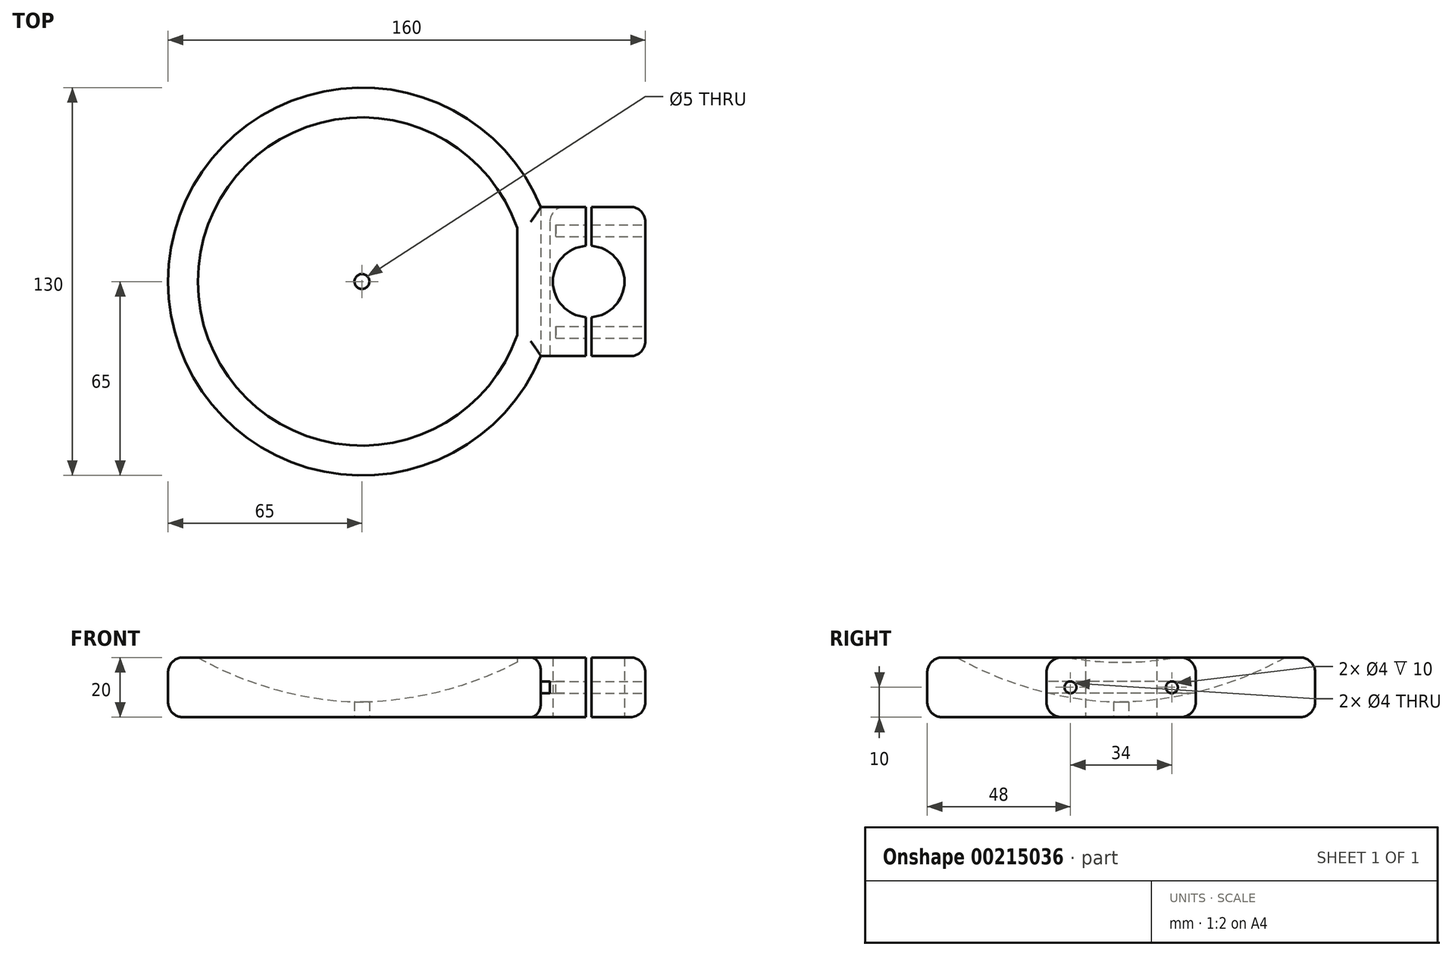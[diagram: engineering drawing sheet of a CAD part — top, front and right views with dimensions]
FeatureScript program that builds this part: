
annotation { "Feature Type Name" : "Feature", "Feature Type Description" : "" }
export const myFeature = defineFeature(function(context is Context, id is Id, definition is map)
    precondition{}
    {
        {
            var Q0;
            Q0=qCreatedBy(makeId("Front.planeOp"),FACE);
            var sketch = newSketch(context, id + "F0", { "sketchPlane" : qUnion([Q0])});
            skLineSegment(sketch, "E0", {"start": v(0, 0) * mm, "end": v(65, 0) * mm});
            skLineSegment(sketch, "E1", {"start": v(65, 0) * mm, "end": v(65, 20) * mm});
            skLineSegment(sketch, "E2", {"start": v(65, 20) * mm, "end": v(55, 20) * mm});
            skArc(sketch, "E3", {"start": v(0, 5) * mm, "mid": v(28.42, 9.13) * mm, "end": v(55, 20) * mm});
            skLineSegment(sketch, "E4", {"start": v(0, 5) * mm, "end": v(0, 0) * mm});
            skPoint(sketch, "E5.end.orphan", {"position": v(-65, 0) * mm});
            skPoint(sketch, "E6.visualSharp", {"position": v(65, 0) * mm});
            skPoint(sketch, "E7.visualSharp", {"position": v(65, 20) * mm});
            skSolve(sketch);
        }
        {
            var Q0;
            Q0=makeQuery(id+"F0.imprint","IMPRINT",FACE,{"disambiguationData":[TD([[makeQuery(id+"F0.imprint","IMPRINT",EDGE,{"derivedFrom":sQuery(id+"F0.wireOp",EDGE,"E0")}),1.0]])]});
            var Q1;
            Q1=sQuery(id+"F0.wireOp",EDGE,"E4");
            revolve(context, id + "F1", {"surfaceOperationType" : NewSurfaceOperationType.NEW, "entities" : qUnion([Q0]), "axis" : qUnion([Q1]), "revolveType" : RevolveType.FULL});
        }
        {
            var Q0;
            Q0=makeQuery(id+"F1.opRevolve","SWEPT_EDGE",EDGE,{"disambiguationData":[OSD([sQuery(id+"F0.wireOp",EDGE,"E1"),sQuery(id+"F0.wireOp",EDGE,"E2")])]});
            var Q1;
            Q1=makeQuery(id+"F1.opRevolve","SWEPT_EDGE",EDGE,{"disambiguationData":[OSD([sQuery(id+"F0.wireOp",EDGE,"E0"),sQuery(id+"F0.wireOp",EDGE,"E1")])]});
            fillet(context, id + "F2", {"entities" : qUnion([Q0, Q1]), "radius" : 5 * mm, "tangentPropagation" : true, "allowEdgeOverflow" : false});
        }
        {
            var Q0;
            Q0=qCreatedBy(makeId("Top.planeOp"),FACE);
            var sketch = newSketch(context, id + "F3", { "sketchPlane" : qUnion([Q0])});
            skLineSegment(sketch, "E8.bottom", {"start": v(52, 25) * mm, "end": v(75, 25) * mm});
            skLineSegment(sketch, "E8.top", {"start": v(52, -25) * mm, "end": v(75, -25) * mm});
            skLineSegment(sketch, "E8.left", {"start": v(52, 25) * mm, "end": v(52, -25) * mm});
            skLineSegment(sketch, "E9.trimOffspring", {"start": v(75, 25) * mm, "end": v(75, -25) * mm});
            skSolve(sketch);
        }
        {
            var Q0;
            Q0=qSketchRegion(id+"F3",true);
            extrude(context, id + "F4", {"entities" : qUnion([Q0]), "operationType" : NewBodyOperationType.ADD, "depth" : 20 * mm});
        }
        {
            var Q0;
            Q0=qCreatedBy(makeId("Top.planeOp"),FACE);
            var sketch = newSketch(context, id + "F5", { "sketchPlane" : qUnion([Q0])});
            skCircle(sketch, "E10", {"center": v(76, 0) * mm, "radius": 12 * mm});
            skSolve(sketch);
        }
        {
            var Q0;
            Q0=qSketchRegion(id+"F5",true);
            extrude(context, id + "F6", {"entities" : qUnion([Q0]), "operationType" : NewBodyOperationType.REMOVE, "depth" : 25 * mm});
        }
        {
            var Q0;
            Q0=qCreatedBy(makeId("Top.planeOp"),FACE);
            var sketch = newSketch(context, id + "F7", { "sketchPlane" : qUnion([Q0])});
            skLineSegment(sketch, "E11.bottom", {"start": v(77, 25) * mm, "end": v(95, 25) * mm});
            skLineSegment(sketch, "E11.top", {"start": v(77, -25) * mm, "end": v(95, -25) * mm});
            skLineSegment(sketch, "E11.left", {"start": v(77, 25) * mm, "end": v(77, -25) * mm});
            skLineSegment(sketch, "E11.right", {"start": v(95, 25) * mm, "end": v(95, -25) * mm});
            skSolve(sketch);
        }
        {
            var Q0;
            Q0=qSketchRegion(id+"F7",true);
            extrude(context, id + "F8", {"entities" : qUnion([Q0]), "depth" : 20 * mm});
        }
        {
            var Q0;
            Q0=qCreatedBy(makeId("Top.planeOp"),FACE);
            var sketch = newSketch(context, id + "F9", { "sketchPlane" : qUnion([Q0])});
            skCircle(sketch, "E12", {"center": v(76, 0) * mm, "radius": 12 * mm});
            skSolve(sketch);
        }
        {
            var Q0;
            Q0=qSketchRegion(id+"F9",true);
            extrude(context, id + "F10", {"entities" : qUnion([Q0]), "operationType" : NewBodyOperationType.REMOVE, "depth" : 25 * mm});
        }
        {
            var Q0;
            Q0=makeQuery(id+"F8.opExtrude","CAP_EDGE",EDGE,{"disambiguationData":[OSD([sQuery(id+"F7.wireOp",EDGE,"E11.top")])],"isStart":false});
            var Q1;
            Q1=makeQuery(id+"F8.opExtrude","CAP_EDGE",EDGE,{"disambiguationData":[OSD([sQuery(id+"F7.wireOp",EDGE,"E11.top")])],"isStart":true});
            var Q2;
            Q2=makeQuery(id+"F8.opExtrude","CAP_EDGE",EDGE,{"disambiguationData":[OSD([sQuery(id+"F7.wireOp",EDGE,"E11.bottom")])],"isStart":false});
            var Q3;
            Q3=makeQuery(id+"F8.opExtrude","CAP_EDGE",EDGE,{"disambiguationData":[OSD([sQuery(id+"F7.wireOp",EDGE,"E11.bottom")])],"isStart":true});
            var Q4;
            Q4=makeQuery(id+"F8.opExtrude","CAP_EDGE",EDGE,{"disambiguationData":[OSD([sQuery(id+"F7.wireOp",EDGE,"E11.right")])],"isStart":false});
            var Q5;
            Q5=makeQuery(id+"F8.opExtrude","CAP_EDGE",EDGE,{"disambiguationData":[OSD([sQuery(id+"F7.wireOp",EDGE,"E11.right")])],"isStart":true});
            var Q6;
            Q6=makeQuery(id+"F8.opExtrude","SWEPT_EDGE",EDGE,{"disambiguationData":[OSD([sQuery(id+"F7.wireOp",EDGE,"E11.top"),sQuery(id+"F7.wireOp",EDGE,"E11.right")])]});
            var Q7;
            Q7=makeQuery(id+"F8.opExtrude","SWEPT_EDGE",EDGE,{"disambiguationData":[OSD([sQuery(id+"F7.wireOp",EDGE,"E11.bottom"),sQuery(id+"F7.wireOp",EDGE,"E11.right")])]});
            fillet(context, id + "F11", {"entities" : qUnion([Q0, Q1, Q2, Q3, Q4, Q5, Q6, Q7]), "radius" : 5 * mm, "tangentPropagation" : true, "allowEdgeOverflow" : false});
        }
        {
            var Q0;
            Q0=makeQuery(id+"F4.opExtrude","CAP_EDGE",EDGE,{"disambiguationData":[OSD([sQuery(id+"F3.wireOp",EDGE,"E8.top")])],"isStart":false});
            var Q1;
            Q1=makeQuery(id+"F4.opExtrude","CAP_EDGE",EDGE,{"disambiguationData":[OSD([sQuery(id+"F3.wireOp",EDGE,"E8.top")])],"isStart":true});
            var Q2;
            Q2=makeQuery(id+"F4.opExtrude","CAP_EDGE",EDGE,{"disambiguationData":[OSD([sQuery(id+"F3.wireOp",EDGE,"E8.bottom")])],"isStart":true});
            var Q3;
            Q3=makeQuery(id+"F4.opExtrude","CAP_EDGE",EDGE,{"disambiguationData":[OSD([sQuery(id+"F3.wireOp",EDGE,"E8.bottom")])],"isStart":false});
            fillet(context, id + "F12", {"entities" : qUnion([Q0, Q1, Q2, Q3]), "radius" : 5 * mm, "allowEdgeOverflow" : false});
        }
        {
            var Q0;
            Q0=makeQuery(id+"F8.opExtrude","SWEPT_FACE",FACE,{"disambiguationData":[OSD([sQuery(id+"F7.wireOp",EDGE,"E11.right")])]});
            var sketch = newSketch(context, id + "F13", { "sketchPlane" : qUnion([Q0])});
            skCircle(sketch, "E13", {"center": v(-17, 10) * mm, "radius": 2 * mm});
            skCircle(sketch, "E14.MirrorC", {"center": v(17, 10) * mm, "radius": 2 * mm});
            skSolve(sketch);
        }
        {
            var Q0;
            Q0=qSketchRegion(id+"F13",true);
            extrude(context, id + "F14", {"entities" : qUnion([Q0]), "operationType" : NewBodyOperationType.REMOVE, "oppositeDirection" : true, "depth" : 30 * mm});
        }
        {
            var Q0;
            {var subQ0=sQuery(id+"F3.wireOp",EDGE,"E9.trimOffspring");var subQ2=sQuery(id+"F3.wireOp",EDGE,"E8.top");Q0=makeQuery(id+"F6.boolean.opBoolean","SPLIT",FACE,{"disambiguationData":[TD([makeQuery(id+"F4.opExtrude","SWEPT_FACE",FACE,{"disambiguationData":[OSD([subQ2])]})])],"derivedFrom":makeQuery(id+"F4.opExtrude","SWEPT_FACE",FACE,{"disambiguationData":[OSD([subQ0])]})});}
            var sketch = newSketch(context, id + "F15", { "sketchPlane" : qUnion([Q0])});
            skCircle(sketch, "E15", {"center": v(-17, 10) * mm, "radius": 2 * mm});
            skCircle(sketch, "E16.MirrorC", {"center": v(17, 10) * mm, "radius": 2 * mm});
            skSolve(sketch);
        }
        {
            var Q0;
            Q0=qSketchRegion(id+"F15",true);
            extrude(context, id + "F16", {"entities" : qUnion([Q0]), "operationType" : NewBodyOperationType.REMOVE, "oppositeDirection" : true, "depth" : 10 * mm});
        }
        {
            var Q0;
            Q0=qCreatedBy(makeId("Top.planeOp"),FACE);
            var sketch = newSketch(context, id + "F17", { "sketchPlane" : qUnion([Q0])});
            skCircle(sketch, "E17", {"center": v(0, 0) * mm, "radius": 2.5 * mm});
            skSolve(sketch);
        }
        {
            var Q0;
            Q0=qSketchRegion(id+"F17",true);
            extrude(context, id + "F18", {"entities" : qUnion([Q0]), "operationType" : NewBodyOperationType.REMOVE, "depth" : 25 * mm});
        }
        {
            var Q0;
            Q0=makeQuery(id+"F4.opExtrude","SWEPT_FACE",FACE,{"disambiguationData":[OSD([sQuery(id+"F3.wireOp",EDGE,"E8.top")])]});
            var sketch = newSketch(context, id + "F19", { "sketchPlane" : qUnion([Q0])});
            skLineSegment(sketch, "E18.bottom", {"start": v(60, 12) * mm, "end": v(63, 12) * mm});
            skLineSegment(sketch, "E18.top", {"start": v(60, 8) * mm, "end": v(63, 8) * mm});
            skLineSegment(sketch, "E18.left", {"start": v(60, 12) * mm, "end": v(60, 8) * mm});
            skLineSegment(sketch, "E18.right", {"start": v(63, 12) * mm, "end": v(63, 8) * mm});
            skSolve(sketch);
        }
        {
            var Q0;
            Q0 = qSketchRegion(id + "F19", true);
            extrude(context, id + "F20", {"entities" : qUnion([Q0]), "operationType" : NewBodyOperationType.REMOVE, "oppositeDirection" : true, "depth" : 80 * mm});
        }
        {
            var Q0;
            Q0=makeQuery(id+"F20.boolean.opBoolean","COPY",EDGE,{"derivedFrom":makeQuery(id+"F20.opExtrude","CAP_EDGE",EDGE,{"disambiguationData":[OSD([sQuery(id+"F19.wireOp",EDGE,"E18.right")])],"isStart":true})});
            var Q1;
            Q1=makeQuery(id+"F20.boolean.opBoolean","INTERSECT",EDGE,{"derivedFrom":[makeQuery(id+"F4.opExtrude","SWEPT_FACE",FACE,{"disambiguationData":[OSD([sQuery(id+"F3.wireOp",EDGE,"E8.bottom")])]}),makeQuery(id+"F20.opExtrude","SWEPT_FACE",FACE,{"disambiguationData":[OSD([sQuery(id+"F19.wireOp",EDGE,"E18.right")])]})]});
            fillet(context, id + "F21", {"entities" : qUnion([Q0, Q1]), "radius" : 5 * mm, "tangentPropagation" : true, "allowEdgeOverflow" : false});
        }
    });
